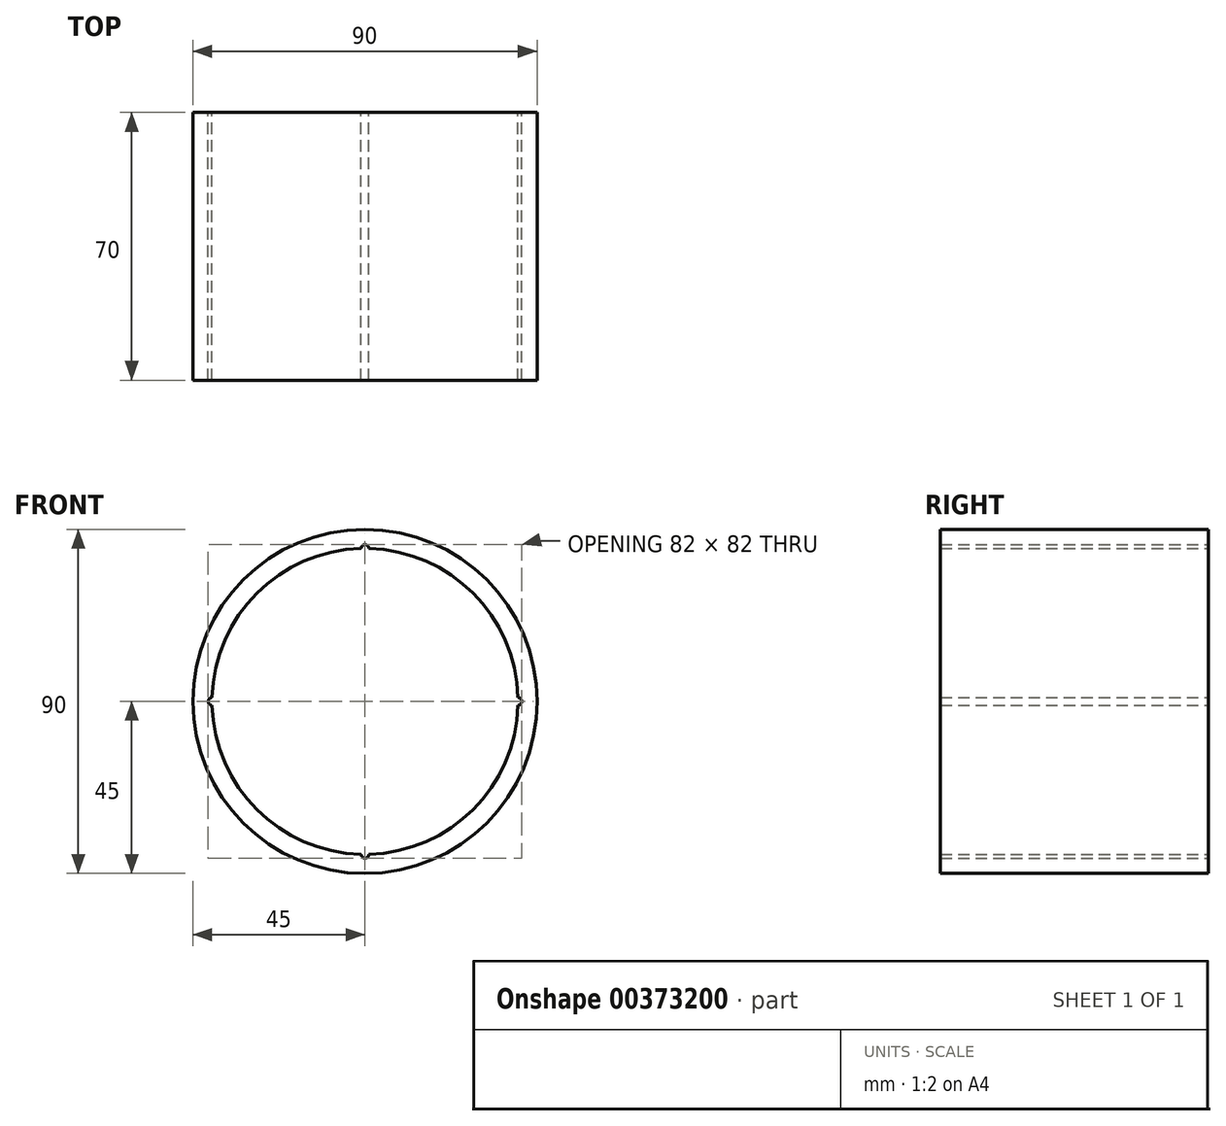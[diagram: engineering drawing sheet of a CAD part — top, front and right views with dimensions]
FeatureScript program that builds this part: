
annotation { "Feature Type Name" : "Feature", "Feature Type Description" : "" }
export const myFeature = defineFeature(function(context is Context, id is Id, definition is map)
    precondition{}
    {
        {
            var Q0;
            Q0=qCreatedBy(makeId("Front.planeOp"),FACE);
            var sketch = newSketch(context, id + "F0", { "sketchPlane" : qUnion([Q0])});
            skCircle(sketch, "E0", {"center": v(0, 0) * mm, "radius": 45 * mm});
            skCircle(sketch, "E1", {"center": v(0, 0) * mm, "radius": 40 * mm});
            skCircle(sketch, "E2", {"center": v(0, 40) * mm, "radius": 1 * mm});
            skCircle(sketch, "E3", {"center": v(0, -40) * mm, "radius": 1 * mm});
            skCircle(sketch, "E4", {"center": v(40, 0) * mm, "radius": 1 * mm});
            skCircle(sketch, "E5", {"center": v(-40, 0) * mm, "radius": 1 * mm});
            skSolve(sketch);
        }
        {
            var Q0;
            Q0=makeQuery(id+"F0.imprint","IMPRINT",FACE,{"disambiguationData":[TD([[makeQuery(id+"F0.imprint","IMPRINT",EDGE,{"derivedFrom":sQuery(id+"F0.wireOp",EDGE,"E0")}),1.0]])]});
            extrude(context, id + "F1", {"entities" : qUnion([Q0]), "endBound" : BoundingType.SYMMETRIC, "depth" : 70 * mm});
        }
    });
